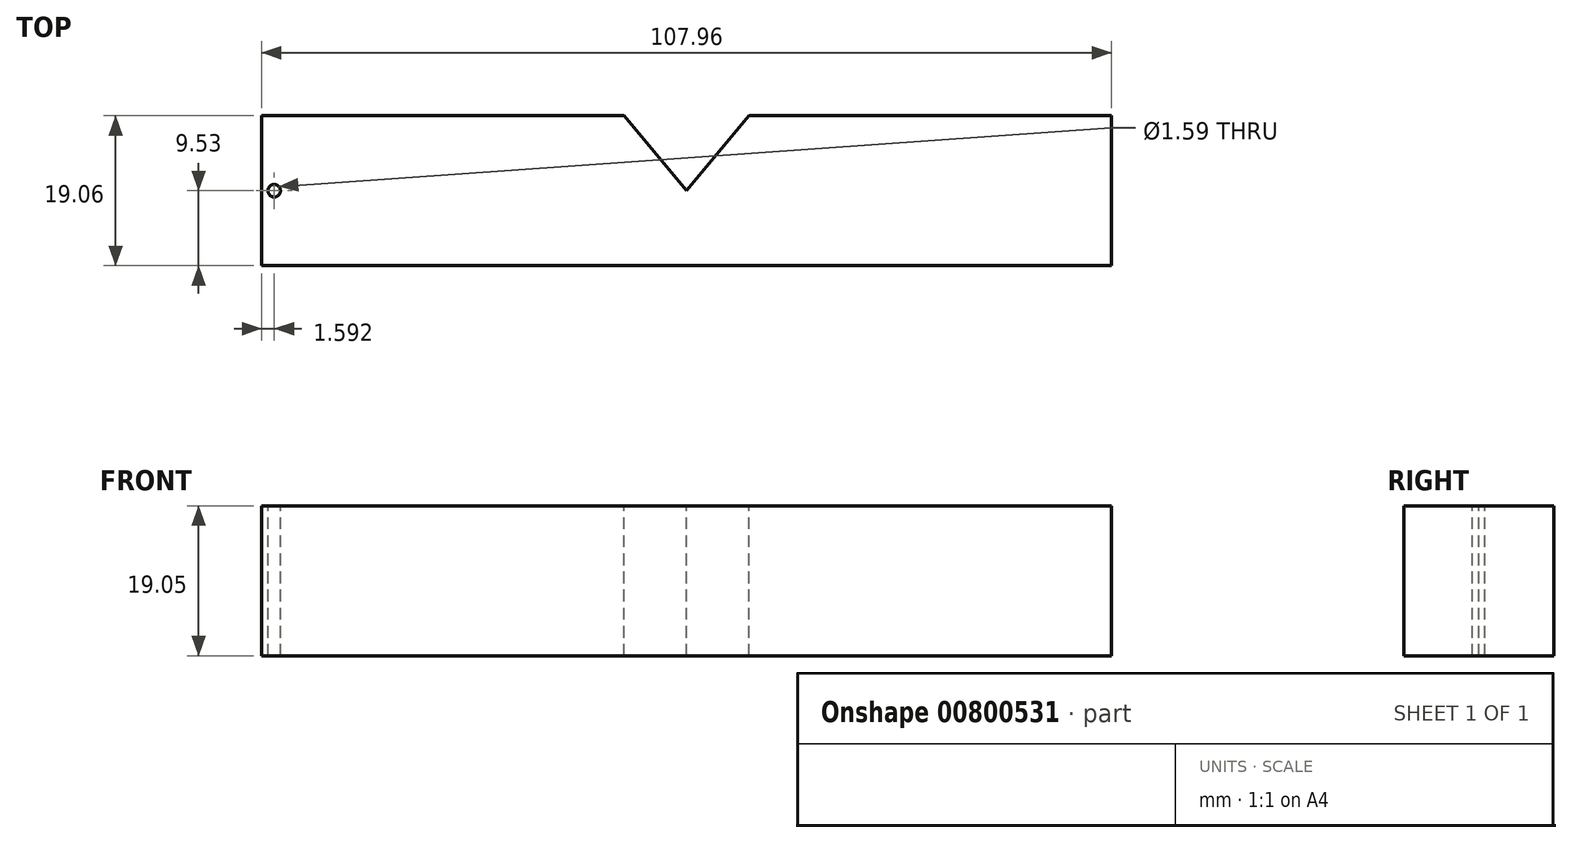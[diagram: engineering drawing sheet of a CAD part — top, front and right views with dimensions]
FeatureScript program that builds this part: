
annotation { "Feature Type Name" : "Feature", "Feature Type Description" : "" }
export const myFeature = defineFeature(function(context is Context, id is Id, definition is map)
    precondition{}
    {
        {
            var Q0;
            Q0=qCreatedBy(makeId("Top.planeOp"),FACE);
            var sketch = newSketch(context, id + "F0", { "sketchPlane" : qUnion([Q0])});
            skLineSegment(sketch, "E0.bottom", {"start": v(-53.98, 9.52) * mm, "end": v(53.98, 9.52) * mm});
            skLineSegment(sketch, "E0.top", {"start": v(-53.98, -9.52) * mm, "end": v(53.98, -9.52) * mm});
            skLineSegment(sketch, "E0.left", {"start": v(-53.98, 9.52) * mm, "end": v(-53.98, -9.52) * mm});
            skLineSegment(sketch, "E0.right", {"start": v(53.98, 9.52) * mm, "end": v(53.98, -9.52) * mm});
            skPoint(sketch, "E0.middle", {"position": v(0, 0) * mm});
            skSolve(sketch);
        }
        {
            var Q0;
            Q0=makeQuery(id+"F0.imprint","IMPRINT",FACE,{"disambiguationData":[TD([[makeQuery(id+"F0.imprint","IMPRINT",EDGE,{"derivedFrom":sQuery(id+"F0.wireOp",EDGE,"E0.bottom")}),-1.0]])]});
            extrude(context, id + "F1", {"entities" : qUnion([Q0]), "oppositeDirection" : true, "depth" : 19.05 * mm, "offsetDistance" : 25.4 * mm});
        }
        {
            var Q0;
            Q0=makeQuery(id+"F1.opExtrude","CAP_FACE",FACE,{"disambiguationData":[OSD([sQuery(id+"F0.wireOp",EDGE,"E0.bottom"),sQuery(id+"F0.wireOp",EDGE,"E0.top"),sQuery(id+"F0.wireOp",EDGE,"E0.left"),sQuery(id+"F0.wireOp",EDGE,"E0.right")])],"isStart":true});
            var sketch = newSketch(context, id + "F2", { "sketchPlane" : qUnion([Q0])});
            skLineSegment(sketch, "E1", {"start": v(0, 0) * mm, "end": v(-7.94, 9.52) * mm});
            skLineSegment(sketch, "E2", {"start": v(0, 0) * mm, "end": v(7.94, 9.52) * mm});
            skSolve(sketch);
        }
        {
            var Q0;
            {var subQ0=sQuery(id+"F2.wireOp",EDGE,"E1");Q0=makeQuery(id+"F2.imprint","IMPRINT",FACE,{"disambiguationData":[TD([[makeQuery(id+"F2.imprint","IMPRINT",EDGE,{"derivedFrom":subQ0}),-1.0]])]});}
            extrude(context, id + "F3", {"entities" : qUnion([Q0]), "operationType" : NewBodyOperationType.REMOVE, "oppositeDirection" : true, "depth" : 25.4 * mm, "offsetDistance" : 25.4 * mm});
        }
        {
            var Q0;
            Q0=makeQuery(id+"F1.opExtrude","CAP_FACE",FACE,{"disambiguationData":[OSD([sQuery(id+"F0.wireOp",EDGE,"E0.bottom"),sQuery(id+"F0.wireOp",EDGE,"E0.top"),sQuery(id+"F0.wireOp",EDGE,"E0.left"),sQuery(id+"F0.wireOp",EDGE,"E0.right")])],"isStart":true});
            var sketch = newSketch(context, id + "F4", { "sketchPlane" : qUnion([Q0])});
            skLineSegment(sketch, "E3", {"start": v(-53.98, 0) * mm, "end": v(-52.39, 0) * mm});
            skSolve(sketch);
        }
        {
            var Q0;
            Q0=sQuery(id+"F4.wireOp",VERTEX,"E3.end");
            var Q1;
            Q1=makeQuery(id+"F1.opExtrude","SWEPT_BODY",BODY,{"disambiguationData":[OSD([sQuery(id+"F0.wireOp",EDGE,"E0.bottom"),sQuery(id+"F0.wireOp",EDGE,"E0.top"),sQuery(id+"F0.wireOp",EDGE,"E0.left"),sQuery(id+"F0.wireOp",EDGE,"E0.right")])]});
            hole(context, id + "F5", {"style" : HoleStyle.SIMPLE, "endStyle" : HoleEndStyle.THROUGH, "holeDiameter" : 1.59 * mm, "majorDiameter" : 6.35 * mm, "isTappedThrough" : true, "tappedDepth" : 12.7 * mm, "tapClearance" : 3, "locations" : qUnion([Q0]), "scope" : qUnion([Q1])});
        }
    });
